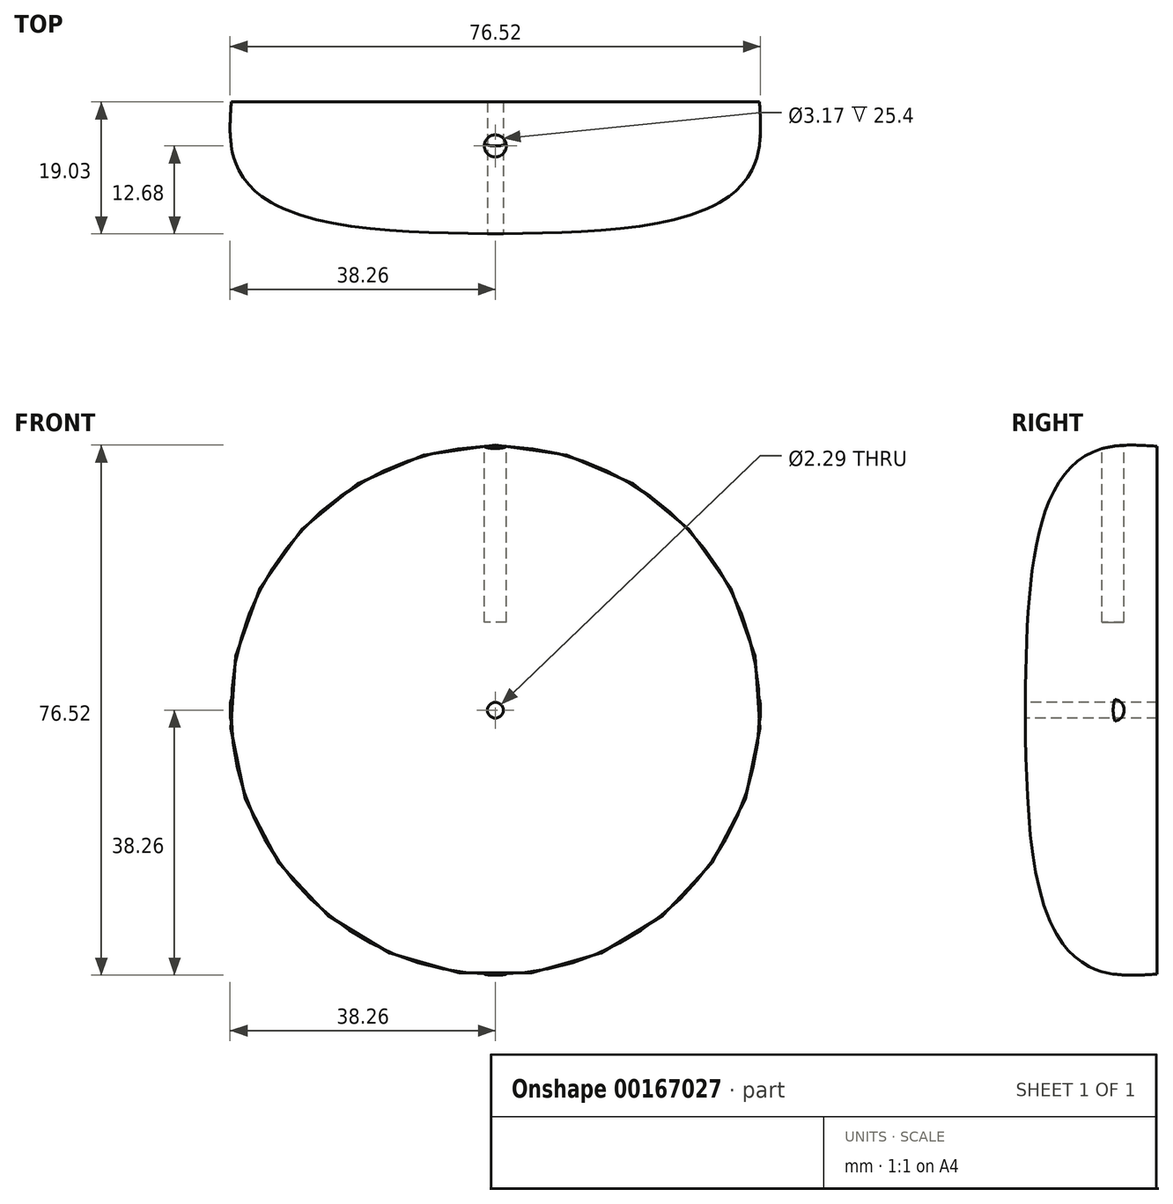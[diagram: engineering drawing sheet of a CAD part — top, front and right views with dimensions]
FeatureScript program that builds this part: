
annotation { "Feature Type Name" : "Feature", "Feature Type Description" : "" }
export const myFeature = defineFeature(function(context is Context, id is Id, definition is map)
    precondition{}
    {
        {
            var Q0;
            Q0=qCreatedBy(makeId("Front.planeOp"),FACE);
            var sketch = newSketch(context, id + "F0", { "sketchPlane" : qUnion([Q0])});
            skCircle(sketch, "E0", {"center": v(0, 0) * mm, "radius": 38.1 * mm});
            skSolve(sketch);
        }
        {
            var Q0;
            Q0=qCreatedBy(makeId("Front.planeOp"),FACE);
            cPlane(context, id + "F1", {"entities" : qUnion([Q0]), "cplaneType" : CPlaneType.OFFSET, "offset" : 6.35 * mm, "width" : 152.4 * mm, "height" : 152.4 * mm});
        }
        {
            var Q0;
            Q0=qCreatedBy(id+"F1.planeOp",FACE);
            var sketch = newSketch(context, id + "F2", { "sketchPlane" : qUnion([Q0])});
            skCircle(sketch, "E1", {"center": v(0, 0) * mm, "radius": 38.1 * mm});
            skPoint(sketch, "E2", {"position": v(0, 38.1) * mm});
            skPoint(sketch, "E3", {"position": v(38.1, 0) * mm});
            skPoint(sketch, "E4", {"position": v(0, -38.1) * mm});
            skPoint(sketch, "E5", {"position": v(-38.1, 0) * mm});
            skSolve(sketch);
        }
        {
            var Q0;
            Q0=qCreatedBy(makeId("Front.planeOp"),FACE);
            cPlane(context, id + "F3", {"entities" : qUnion([Q0]), "cplaneType" : CPlaneType.OFFSET, "offset" : 19.05 * mm, "width" : 152.4 * mm, "height" : 152.4 * mm});
        }
        {
            var Q0;
            Q0=qCreatedBy(id+"F3.planeOp",FACE);
            var sketch = newSketch(context, id + "F4", { "sketchPlane" : qUnion([Q0])});
            skPoint(sketch, "E6", {"position": v(0, 0) * mm});
            skSolve(sketch);
        }
        {
            var Q0;
            Q0=makeQuery(id+"F0.imprint","IMPRINT",FACE,{"disambiguationData":[TD([[makeQuery(id+"F0.imprint","IMPRINT",EDGE,{"derivedFrom":sQuery(id+"F0.wireOp",EDGE,"E0")}),1.0]])]});
            var Q1;
            Q1=makeQuery(id+"F2.imprint","IMPRINT",FACE,{"disambiguationData":[TD([[makeQuery(id+"F2.imprint","IMPRINT",EDGE,{"derivedFrom":sQuery(id+"F2.wireOp",EDGE,"E1")}),1.0]])]});
            var Q2;
            Q2=sQuery(id+"F4.wireOp",VERTEX,"E6");
            loft(context, id + "F5", {"sheetProfilesArray" : [{ "sheetProfileEntities" : qUnion([Q0]) }, { "sheetProfileEntities" : qUnion([Q1]) }, { "sheetProfileEntities" : qUnion([Q2]) }]});
        }
        {
            var Q0;
            Q0=qCreatedBy(makeId("Top.planeOp"),FACE);
            cPlane(context, id + "F6", {"entities" : qUnion([Q0]), "cplaneType" : CPlaneType.OFFSET, "offset" : 38.1 * mm, "width" : 152.4 * mm, "height" : 152.4 * mm});
        }
        {
            var Q0;
            Q0=qCreatedBy(makeId("Right.planeOp"),FACE);
            cPlane(context, id + "F7", {"entities" : qUnion([Q0]), "cplaneType" : CPlaneType.OFFSET, "offset" : 38.1 * mm, "width" : 152.4 * mm, "height" : 152.4 * mm});
        }
        {
            var Q0;
            Q0=qCreatedBy(id+"F7.planeOp",FACE);
            var sketch = newSketch(context, id + "F8", { "sketchPlane" : qUnion([Q0])});
            skPoint(sketch, "E7", {"position": v(-6.35, 0) * mm});
            skCircle(sketch, "E8", {"center": v(-6.35, 0) * mm, "radius": 1.59 * mm});
            skSolve(sketch);
        }
        {
            var Q0;
            Q0 = qSketchRegion(id + "F8", true);
            extrude(context, id + "F9", {"entities" : qUnion([Q0]), "operationType" : NewBodyOperationType.REMOVE, "depth" : 25.4 * mm});
        }
        {
            var Q0;
            Q0=qCreatedBy(id+"F6.planeOp",FACE);
            var sketch = newSketch(context, id + "F10", { "sketchPlane" : qUnion([Q0])});
            skPoint(sketch, "E9", {"position": v(0, -6.35) * mm});
            skCircle(sketch, "E10", {"center": v(0, -6.35) * mm, "radius": 1.59 * mm});
            skSolve(sketch);
        }
        {
            var Q0;
            Q0 = qSketchRegion(id + "F10", true);
            extrude(context, id + "F11", {"entities" : qUnion([Q0]), "operationType" : NewBodyOperationType.REMOVE, "oppositeDirection" : true, "depth" : 25.4 * mm});
        }
        {
            var Q0;
            Q0=qCreatedBy(makeId("Top.planeOp"),FACE);
            cPlane(context, id + "F12", {"entities" : qUnion([Q0]), "cplaneType" : CPlaneType.OFFSET, "offset" : 38.1 * mm, "oppositeDirection" : true, "width" : 152.4 * mm, "height" : 152.4 * mm});
        }
        {
            var Q0;
            Q0=qCreatedBy(id+"F12.planeOp",FACE);
            var sketch = newSketch(context, id + "F13", { "sketchPlane" : qUnion([Q0])});
            skCircle(sketch, "E11", {"center": v(0, -6.35) * mm, "radius": 1.59 * mm});
            skSolve(sketch);
        }
        {
            var Q0;
            Q0 = qSketchRegion(id + "F13", true);
            extrude(context, id + "F14", {"entities" : qUnion([Q0]), "operationType" : NewBodyOperationType.REMOVE, "oppositeDirection" : true, "depth" : 25.4 * mm});
        }
        {
            var Q0;
            Q0=qCreatedBy(makeId("Right.planeOp"),FACE);
            cPlane(context, id + "F15", {"entities" : qUnion([Q0]), "cplaneType" : CPlaneType.OFFSET, "offset" : 38.1 * mm, "oppositeDirection" : true, "width" : 152.4 * mm, "height" : 152.4 * mm});
        }
        {
            var Q0;
            Q0=qCreatedBy(id+"F15.planeOp",FACE);
            var sketch = newSketch(context, id + "F16", { "sketchPlane" : qUnion([Q0])});
            skPoint(sketch, "E12", {"position": v(-6.35, 0) * mm});
            skCircle(sketch, "E13", {"center": v(-6.35, 0) * mm, "radius": 1.59 * mm});
            skSolve(sketch);
        }
        {
            var Q0;
            Q0 = qSketchRegion(id + "F16", true);
            extrude(context, id + "F17", {"entities" : qUnion([Q0]), "operationType" : NewBodyOperationType.REMOVE, "oppositeDirection" : true, "depth" : 25.4 * mm});
        }
        {
            var Q0;
            Q0=qCreatedBy(id+"F3.planeOp",FACE);
            var sketch = newSketch(context, id + "F18", { "sketchPlane" : qUnion([Q0])});
            skCircle(sketch, "E14", {"center": v(0, 0) * mm, "radius": 1.14 * mm});
            skSolve(sketch);
        }
        {
            var Q0;
            Q0 = qSketchRegion(id + "F18", true);
            extrude(context, id + "F19", {"entities" : qUnion([Q0]), "operationType" : NewBodyOperationType.REMOVE, "oppositeDirection" : true, "depth" : 25.4 * mm});
        }
    });
